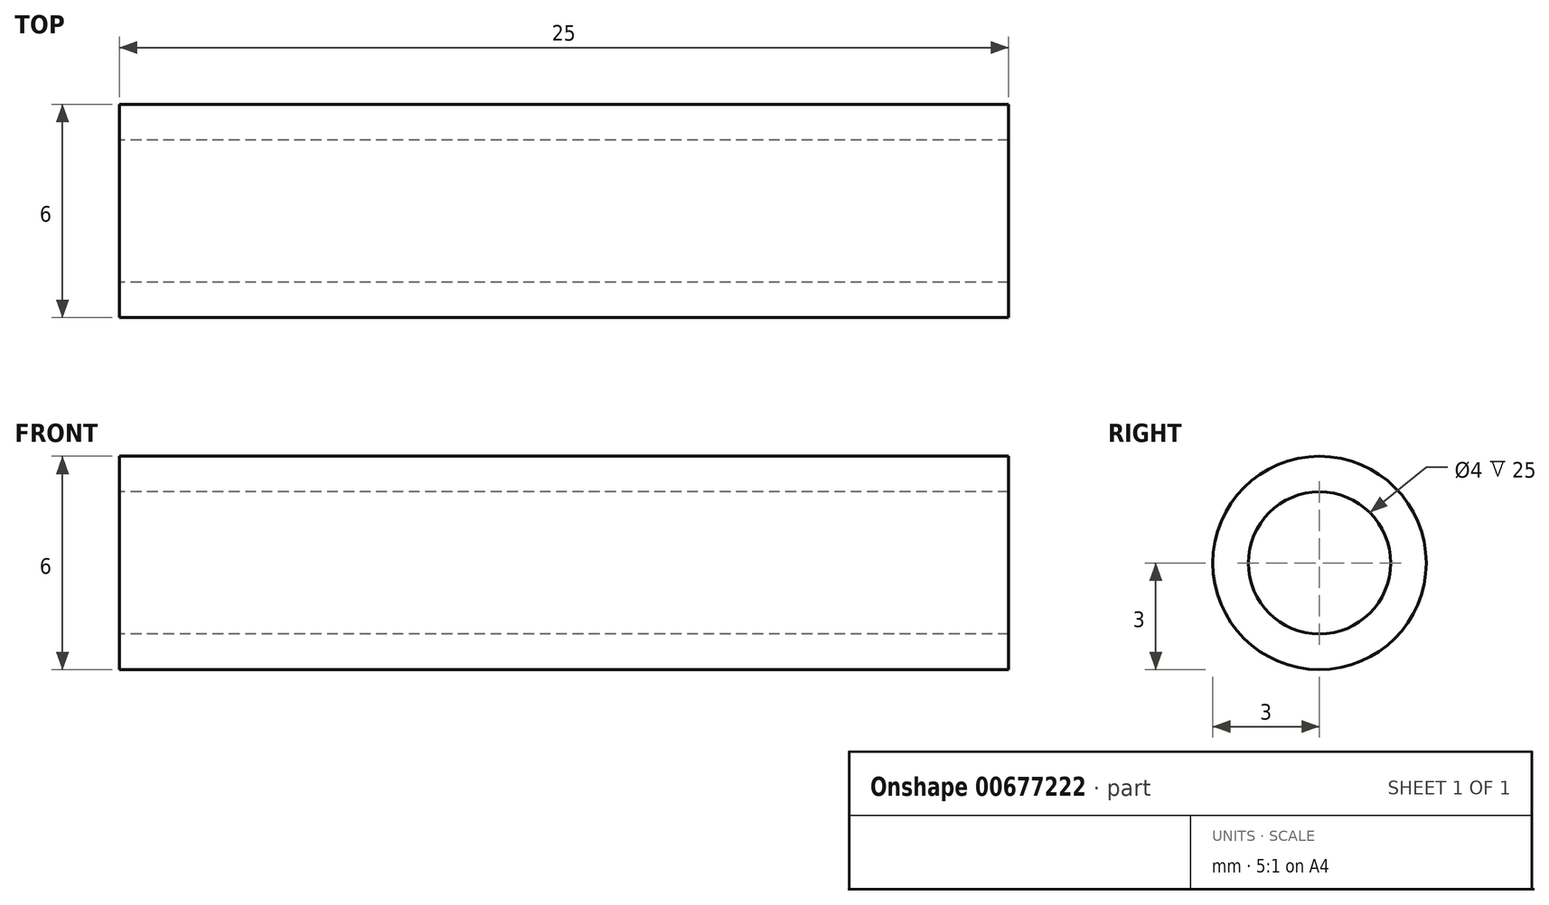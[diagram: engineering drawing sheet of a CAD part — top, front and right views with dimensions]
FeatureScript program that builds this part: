
annotation { "Feature Type Name" : "Feature", "Feature Type Description" : "" }
export const myFeature = defineFeature(function(context is Context, id is Id, definition is map)
    precondition{}
    {
        {
            var Q0;
            Q0=qCreatedBy(makeId("Right.planeOp"),FACE);
            var sketch = newSketch(context, id + "F0", { "sketchPlane" : qUnion([Q0])});
            skCircle(sketch, "E0", {"center": v(0, 0) * mm, "radius": 2 * mm});
            skCircle(sketch, "E1", {"center": v(0, 0) * mm, "radius": 3 * mm});
            skSolve(sketch);
        }
        {
            var Q0;
            Q0 = qSketchRegion(id + "F0", true);
            extrude(context, id + "F1", {"entities" : qUnion([Q0]), "depth" : 25 * mm, "offsetDistance" : 25 * mm});
        }
    });
